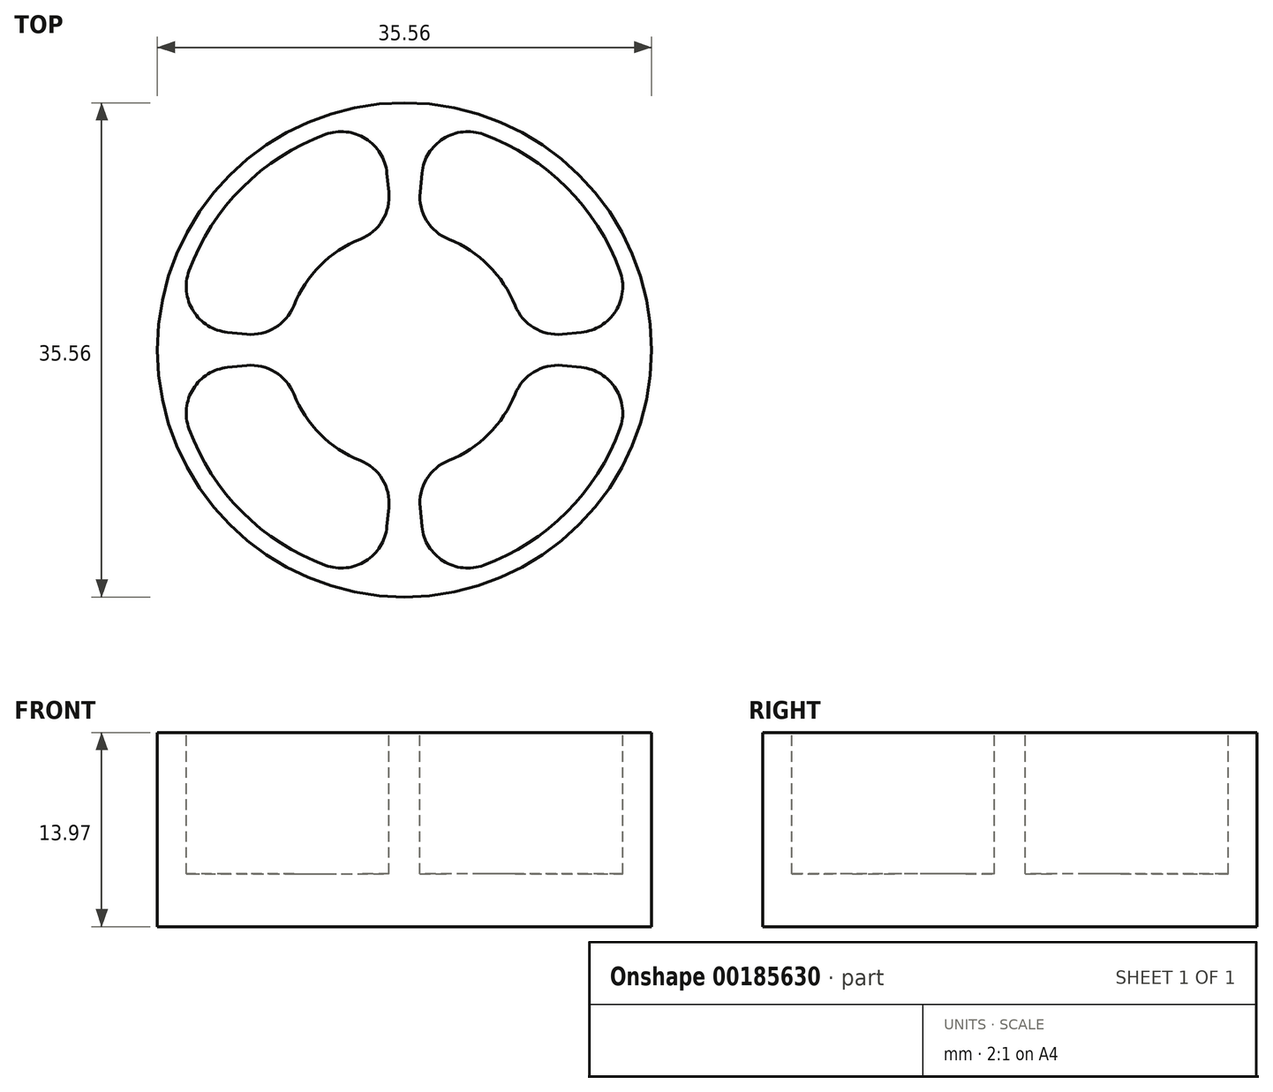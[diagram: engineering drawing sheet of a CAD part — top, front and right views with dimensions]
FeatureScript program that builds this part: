
annotation { "Feature Type Name" : "Feature", "Feature Type Description" : "" }
export const myFeature = defineFeature(function(context is Context, id is Id, definition is map)
    precondition{}
    {
        {
            var Q0;
            Q0=qCreatedBy(makeId("Top.planeOp"),FACE);
            var sketch = newSketch(context, id + "F0", { "sketchPlane" : qUnion([Q0])});
            skCircle(sketch, "E0", {"center": v(0, 0) * mm, "radius": 17.78 * mm});
            skCircle(sketch, "E1", {"center": v(0, 0) * mm, "radius": 7.3 * mm});
            skArc(sketch, "E2", {"start": v(-7.96, -3.19) * mm, "mid": v(-6.06, -6.06) * mm, "end": v(-3.19, -7.96) * mm});
            skArc(sketch, "E3", {"start": v(-15.5, -5.69) * mm, "mid": v(-11.67, -11.67) * mm, "end": v(-5.69, -15.5) * mm});
            skLineSegment(sketch, "E4", {"start": v(-11.35, 1.13) * mm, "end": v(-12.73, 1.26) * mm});
            skLineSegment(sketch, "E5", {"start": v(-11.35, -1.13) * mm, "end": v(-12.73, -1.26) * mm});
            skLineSegment(sketch, "E6", {"start": v(11.35, 1.13) * mm, "end": v(12.73, 1.26) * mm});
            skLineSegment(sketch, "E7", {"start": v(11.35, -1.13) * mm, "end": v(12.73, -1.26) * mm});
            skLineSegment(sketch, "E8", {"start": v(-1.13, 11.35) * mm, "end": v(-1.26, 12.73) * mm});
            skLineSegment(sketch, "E9", {"start": v(1.13, 11.35) * mm, "end": v(1.26, 12.73) * mm});
            skLineSegment(sketch, "E10", {"start": v(-1.13, -11.35) * mm, "end": v(-1.26, -12.73) * mm});
            skLineSegment(sketch, "E11", {"start": v(1.13, -11.35) * mm, "end": v(1.26, -12.73) * mm});
            skArc(sketch, "E12.trimOffspring", {"start": v(-3.19, 7.96) * mm, "mid": v(-6.06, 6.06) * mm, "end": v(-7.96, 3.19) * mm});
            skArc(sketch, "E13.trimOffspring", {"start": v(-5.69, 15.5) * mm, "mid": v(-11.67, 11.67) * mm, "end": v(-15.5, 5.69) * mm});
            skArc(sketch, "E14.trimOffspring", {"start": v(7.96, 3.19) * mm, "mid": v(6.06, 6.06) * mm, "end": v(3.19, 7.96) * mm});
            skArc(sketch, "E15.trimOffspring", {"start": v(15.5, 5.69) * mm, "mid": v(11.67, 11.67) * mm, "end": v(5.69, 15.5) * mm});
            skArc(sketch, "E16.trimOffspring", {"start": v(3.19, -7.96) * mm, "mid": v(6.06, -6.06) * mm, "end": v(7.96, -3.19) * mm});
            skArc(sketch, "E17.trimOffspring", {"start": v(5.69, -15.5) * mm, "mid": v(11.67, -11.67) * mm, "end": v(15.5, -5.69) * mm});
            skPoint(sketch, "E18.visualSharp", {"position": v(-16.43, 1.63) * mm});
            skArc(sketch, "E18.filletArc", {"start": v(-15.5, 5.69) * mm, "mid": v(-15.2, 2.8) * mm, "end": v(-12.73, 1.26) * mm});
            skPoint(sketch, "E19.visualSharp", {"position": v(-8.53, 0.85) * mm});
            skArc(sketch, "E19.filletArc", {"start": v(-11.35, 1.13) * mm, "mid": v(-9.31, 1.59) * mm, "end": v(-7.96, 3.19) * mm});
            skPoint(sketch, "E20.visualSharp", {"position": v(-1.63, 16.43) * mm});
            skArc(sketch, "E20.filletArc", {"start": v(-1.26, 12.73) * mm, "mid": v(-2.8, 15.2) * mm, "end": v(-5.69, 15.5) * mm});
            skPoint(sketch, "E21.visualSharp", {"position": v(-0.85, 8.53) * mm});
            skArc(sketch, "E21.filletArc", {"start": v(-3.19, 7.96) * mm, "mid": v(-1.59, 9.31) * mm, "end": v(-1.13, 11.35) * mm});
            skPoint(sketch, "E22.visualSharp", {"position": v(1.63, 16.43) * mm});
            skArc(sketch, "E22.filletArc", {"start": v(5.69, 15.5) * mm, "mid": v(2.8, 15.2) * mm, "end": v(1.26, 12.73) * mm});
            skPoint(sketch, "E23.visualSharp", {"position": v(0.85, 8.53) * mm});
            skArc(sketch, "E23.filletArc", {"start": v(1.13, 11.35) * mm, "mid": v(1.59, 9.31) * mm, "end": v(3.19, 7.96) * mm});
            skPoint(sketch, "E24.visualSharp", {"position": v(8.53, 0.85) * mm});
            skArc(sketch, "E24.filletArc", {"start": v(7.96, 3.19) * mm, "mid": v(9.31, 1.59) * mm, "end": v(11.35, 1.13) * mm});
            skPoint(sketch, "E25.visualSharp", {"position": v(16.43, 1.63) * mm});
            skArc(sketch, "E25.filletArc", {"start": v(12.73, 1.26) * mm, "mid": v(15.2, 2.8) * mm, "end": v(15.5, 5.69) * mm});
            skPoint(sketch, "E26.visualSharp", {"position": v(8.53, -0.85) * mm});
            skArc(sketch, "E26.filletArc", {"start": v(11.35, -1.13) * mm, "mid": v(9.31, -1.59) * mm, "end": v(7.96, -3.19) * mm});
            skPoint(sketch, "E27.visualSharp", {"position": v(16.43, -1.63) * mm});
            skArc(sketch, "E27.filletArc", {"start": v(15.5, -5.69) * mm, "mid": v(15.2, -2.8) * mm, "end": v(12.73, -1.26) * mm});
            skPoint(sketch, "E28.visualSharp", {"position": v(0.85, -8.53) * mm});
            skArc(sketch, "E28.filletArc", {"start": v(3.19, -7.96) * mm, "mid": v(1.59, -9.31) * mm, "end": v(1.13, -11.35) * mm});
            skPoint(sketch, "E29.visualSharp", {"position": v(1.63, -16.43) * mm});
            skArc(sketch, "E29.filletArc", {"start": v(1.26, -12.73) * mm, "mid": v(2.8, -15.2) * mm, "end": v(5.69, -15.5) * mm});
            skPoint(sketch, "E30.visualSharp", {"position": v(-0.85, -8.53) * mm});
            skArc(sketch, "E30.filletArc", {"start": v(-1.13, -11.35) * mm, "mid": v(-1.59, -9.31) * mm, "end": v(-3.19, -7.96) * mm});
            skPoint(sketch, "E31.visualSharp", {"position": v(-1.63, -16.43) * mm});
            skArc(sketch, "E31.filletArc", {"start": v(-5.69, -15.5) * mm, "mid": v(-2.8, -15.2) * mm, "end": v(-1.26, -12.73) * mm});
            skPoint(sketch, "E32.visualSharp", {"position": v(-16.43, -1.63) * mm});
            skArc(sketch, "E32.filletArc", {"start": v(-12.73, -1.26) * mm, "mid": v(-15.2, -2.8) * mm, "end": v(-15.5, -5.69) * mm});
            skPoint(sketch, "E33.visualSharp", {"position": v(-8.53, -0.85) * mm});
            skArc(sketch, "E33.filletArc", {"start": v(-7.96, -3.19) * mm, "mid": v(-9.31, -1.59) * mm, "end": v(-11.35, -1.13) * mm});
            skSolve(sketch);
        }
        {
            var Q0;
            Q0=makeQuery(id+"F0.imprint","IMPRINT",FACE,{"disambiguationData":[TD([[makeQuery(id+"F0.imprint","IMPRINT",EDGE,{"derivedFrom":sQuery(id+"F0.wireOp",EDGE,"E0")}),1.0]])]});
            var Q1;
            Q1=makeQuery(id+"F0.imprint","IMPRINT",FACE,{"disambiguationData":[TD([[makeQuery(id+"F0.imprint","IMPRINT",EDGE,{"derivedFrom":sQuery(id+"F0.wireOp",EDGE,"E2")}),-1.0]])]});
            var Q2;
            Q2=makeQuery(id+"F0.imprint","IMPRINT",FACE,{"disambiguationData":[TD([[makeQuery(id+"F0.imprint","IMPRINT",EDGE,{"derivedFrom":sQuery(id+"F0.wireOp",EDGE,"E1")}),1.0]])]});
            var Q3;
            Q3=makeQuery(id+"F0.imprint","IMPRINT",FACE,{"disambiguationData":[TD([[makeQuery(id+"F0.imprint","IMPRINT",EDGE,{"derivedFrom":sQuery(id+"F0.wireOp",EDGE,"E4")}),-1.0]])]});
            var Q4;
            Q4=makeQuery(id+"F0.imprint","IMPRINT",FACE,{"disambiguationData":[TD([[makeQuery(id+"F0.imprint","IMPRINT",EDGE,{"derivedFrom":sQuery(id+"F0.wireOp",EDGE,"E6")}),1.0]])]});
            var Q5;
            Q5=makeQuery(id+"F0.imprint","IMPRINT",FACE,{"disambiguationData":[TD([[makeQuery(id+"F0.imprint","IMPRINT",EDGE,{"derivedFrom":sQuery(id+"F0.wireOp",EDGE,"E7")}),-1.0]])]});
            extrude(context, id + "F1", {"entities" : qUnion([Q0, Q1, Q2, Q3, Q4, Q5]), "oppositeDirection" : true, "depth" : 13.97 * mm});
        }
        {
            var Q0;
            Q0=makeQuery(id+"F0.imprint","IMPRINT",FACE,{"disambiguationData":[TD([[makeQuery(id+"F0.imprint","IMPRINT",EDGE,{"derivedFrom":sQuery(id+"F0.wireOp",EDGE,"E2")}),-1.0]])]});
            var Q1;
            Q1=makeQuery(id+"F0.imprint","IMPRINT",FACE,{"disambiguationData":[TD([[makeQuery(id+"F0.imprint","IMPRINT",EDGE,{"derivedFrom":sQuery(id+"F0.wireOp",EDGE,"E4")}),-1.0]])]});
            var Q2;
            Q2=makeQuery(id+"F0.imprint","IMPRINT",FACE,{"disambiguationData":[TD([[makeQuery(id+"F0.imprint","IMPRINT",EDGE,{"derivedFrom":sQuery(id+"F0.wireOp",EDGE,"E6")}),1.0]])]});
            var Q3;
            Q3=makeQuery(id+"F0.imprint","IMPRINT",FACE,{"disambiguationData":[TD([[makeQuery(id+"F0.imprint","IMPRINT",EDGE,{"derivedFrom":sQuery(id+"F0.wireOp",EDGE,"E7")}),-1.0]])]});
            extrude(context, id + "F2", {"entities" : qUnion([Q0, Q1, Q2, Q3]), "operationType" : NewBodyOperationType.REMOVE, "oppositeDirection" : true, "depth" : 10.16 * mm});
        }
    });
